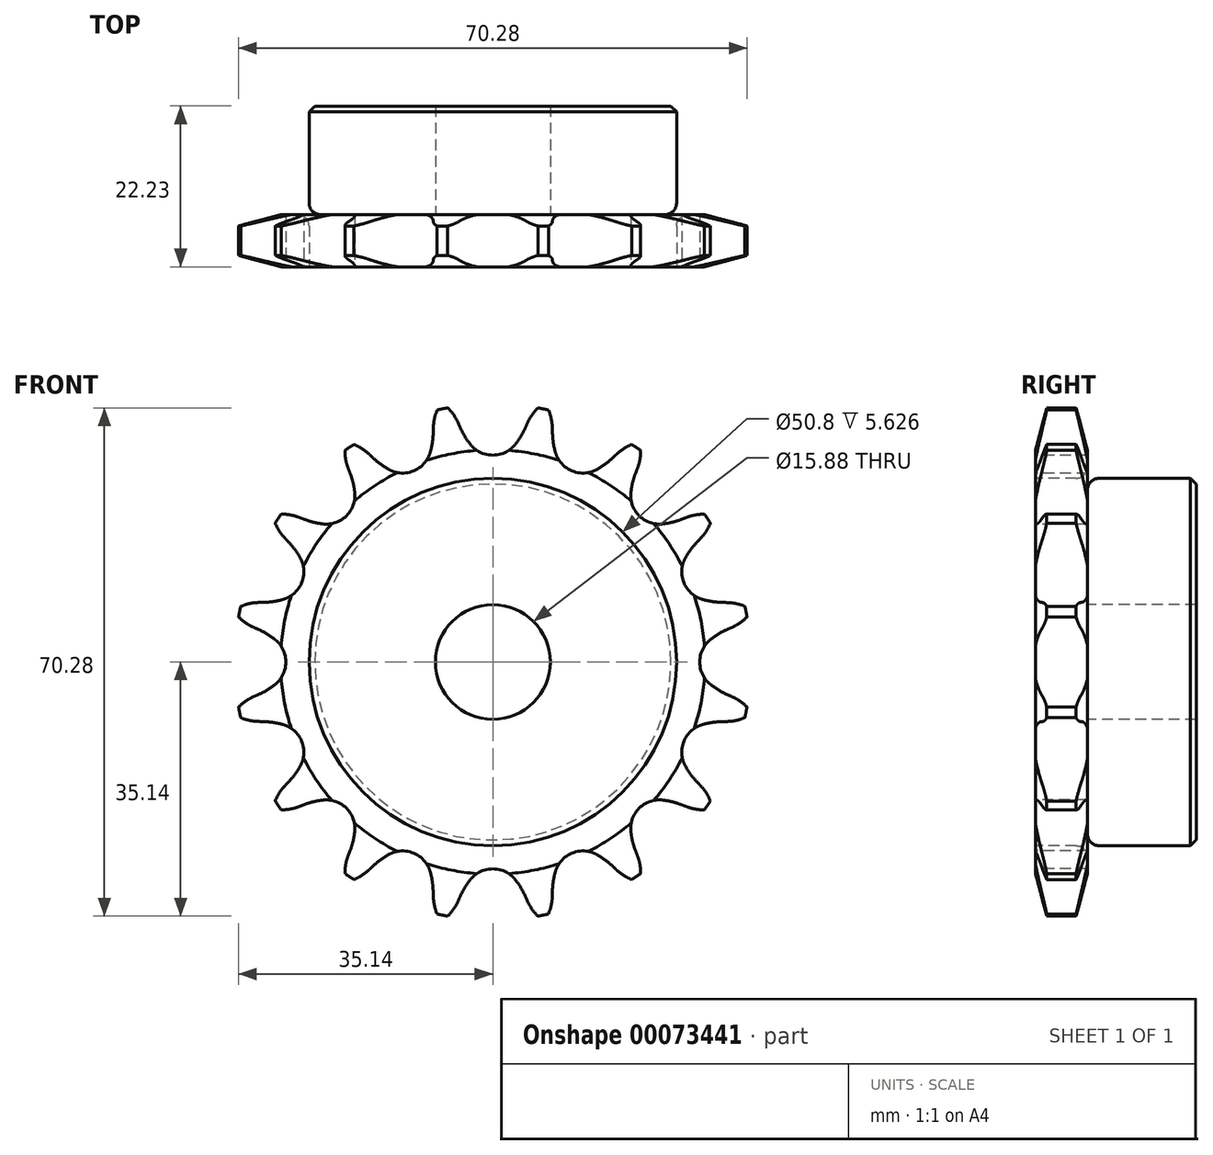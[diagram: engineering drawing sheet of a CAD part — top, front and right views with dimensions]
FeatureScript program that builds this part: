
annotation { "Feature Type Name" : "Feature", "Feature Type Description" : "" }
export const myFeature = defineFeature(function(context is Context, id is Id, definition is map)
    precondition{}
    {
        {
            var Q0;
            Q0=qCreatedBy(makeId("Right.planeOp"),FACE);
            var sketch = newSketch(context, id + "F0", { "sketchPlane" : qUnion([Q0])});
            skLineSegment(sketch, "E0", {"start": v(0, 0) * mm, "end": v(22.23, 0) * mm, "construction": true});
            skLineSegment(sketch, "E1.bottom", {"start": v(0, 7.94) * mm, "end": v(7.21, 7.94) * mm});
            skLineSegment(sketch, "E1.top", {"start": v(0, 35.69) * mm, "end": v(7.21, 35.69) * mm});
            skLineSegment(sketch, "E1.left", {"start": v(0, 7.94) * mm, "end": v(0, 35.69) * mm});
            skLineSegment(sketch, "E1.right", {"start": v(7.21, 7.94) * mm, "end": v(7.21, 35.69) * mm});
            skLineSegment(sketch, "E2.bottom", {"start": v(0, 7.94) * mm, "end": v(22.23, 7.94) * mm});
            skLineSegment(sketch, "E2.top", {"start": v(0, 25.4) * mm, "end": v(22.23, 25.4) * mm});
            skLineSegment(sketch, "E2.left", {"start": v(0, 7.94) * mm, "end": v(0, 25.4) * mm});
            skLineSegment(sketch, "E2.right", {"start": v(22.23, 7.94) * mm, "end": v(22.23, 25.4) * mm});
            skLineSegment(sketch, "E3.MirrorCS", {"start": v(0, -7.94) * mm, "end": v(7.21, -7.94) * mm});
            skLineSegment(sketch, "E4.MirrorCS", {"start": v(0, -25.4) * mm, "end": v(22.23, -25.4) * mm});
            skLineSegment(sketch, "E5.MirrorCS", {"start": v(0, -7.94) * mm, "end": v(22.23, -7.94) * mm});
            skLineSegment(sketch, "E6.MirrorCS", {"start": v(7.21, -7.94) * mm, "end": v(7.21, -35.69) * mm});
            skLineSegment(sketch, "E7.MirrorCS", {"start": v(0, -7.94) * mm, "end": v(0, -35.69) * mm});
            skLineSegment(sketch, "E8.MirrorCS", {"start": v(22.23, -7.94) * mm, "end": v(22.23, -25.4) * mm});
            skLineSegment(sketch, "E9.MirrorCS", {"start": v(0, -7.94) * mm, "end": v(0, -25.4) * mm});
            skLineSegment(sketch, "E10.MirrorCS", {"start": v(0, -35.69) * mm, "end": v(7.21, -35.69) * mm});
            skSolve(sketch);
        }
        {
            var Q0;
            {var subQ0=sQuery(id+"F0.wireOp",EDGE,"E1.top");Q0=makeQuery(id+"F0.imprint","IMPRINT",FACE,{"disambiguationData":[TD([[makeQuery(id+"F0.imprint","IMPRINT",EDGE,{"derivedFrom":subQ0}),-1.0]])]});}
            var Q1;
            {var subQ5=sQuery(id+"F0.wireOp",EDGE,"E2.left");Q1=makeQuery(id+"F0.imprint","IMPRINT",FACE,{"disambiguationData":[TD([[makeQuery(id+"F0.imprint","IMPRINT",EDGE,{"derivedFrom":subQ5}),-1.0]])]});}
            var Q2;
            {var subQ5=sQuery(id+"F0.wireOp",EDGE,"E2.right");Q2=makeQuery(id+"F0.imprint","IMPRINT",FACE,{"disambiguationData":[TD([[makeQuery(id+"F0.imprint","IMPRINT",EDGE,{"derivedFrom":subQ5}),1.0]])]});}
            var Q3;
            Q3=sQuery(id+"F0.wireOp",EDGE,"E0");
            revolve(context, id + "F1", {"entities" : qUnion([Q0, Q1, Q2]), "axis" : qUnion([Q3]), "revolveType" : RevolveType.FULL});
        }
        {
            var Q0;
            Q0=makeQuery(id+"F1.opRevolve","SWEPT_EDGE",EDGE,{"disambiguationData":[OSD([sQuery(id+"F0.wireOp",EDGE,"E1.right"),sQuery(id+"F0.wireOp",EDGE,"E2.top")])]});
            fillet(context, id + "F2", {"entities" : qUnion([Q0]), "radius" : 1.59 * mm, "tangentPropagation" : true, "allowEdgeOverflow" : false});
        }
        {
            var Q0;
            Q0=makeQuery(id+"F1.opRevolve","SWEPT_EDGE",EDGE,{"disambiguationData":[OSD([sQuery(id+"F0.wireOp",EDGE,"E2.top"),sQuery(id+"F0.wireOp",EDGE,"E2.right")])]});
            chamfer(context, id + "F3", {"entities" : qUnion([Q0]), "width" : 0.8 * mm, "tangentPropagation" : true});
        }
        {
            var Q0;
            Q0=makeQuery(id+"F1.opRevolve","SWEPT_EDGE",EDGE,{"disambiguationData":[OSD([sQuery(id+"F0.wireOp",EDGE,"E1.top"),sQuery(id+"F0.wireOp",EDGE,"E1.left")])]});
            var Q1;
            Q1=makeQuery(id+"F1.opRevolve","SWEPT_EDGE",EDGE,{"disambiguationData":[OSD([sQuery(id+"F0.wireOp",EDGE,"E1.top"),sQuery(id+"F0.wireOp",EDGE,"E1.right")])]});
            chamfer(context, id + "F4", {"entities" : qUnion([Q0, Q1]), "chamferType" : ChamferType.TWO_OFFSETS, "width1" : 6.35 * mm, "oppositeDirection" : false, "width2" : 1.57 * mm, "tangentPropagation" : true});
        }
        {
            var Q0;
            Q0=makeQuery(id+"F1.opRevolve","SWEPT_FACE",FACE,{"disambiguationData":[OSD([sQuery(id+"F0.wireOp",EDGE,"E1.left"),sQuery(id+"F0.wireOp",EDGE,"E2.left")])]});
            var sketch = newSketch(context, id + "F5", { "sketchPlane" : qUnion([Q0])});
            skArc(sketch, "E11", {"start": v(-4.8, 33.1) * mm, "mid": v(-5.78, 34.65) * mm, "end": v(-7.13, 35.87) * mm});
            skLineSegment(sketch, "E12", {"start": v(-4.45, 32.3) * mm, "end": v(-4.8, 33.1) * mm});
            skArc(sketch, "E13", {"start": v(-4.45, 32.3) * mm, "mid": v(-3.84, 31.15) * mm, "end": v(-3.1, 30.08) * mm});
            skArc(sketch, "E14", {"start": v(-3.1, 30.08) * mm, "mid": v(0.01, 28.6) * mm, "end": v(3.1, 30.1) * mm});
            skArc(sketch, "E15.MirrorCS", {"start": v(4.46, 32.32) * mm, "mid": v(3.85, 31.17) * mm, "end": v(3.1, 30.1) * mm});
            skLineSegment(sketch, "E16.MirrorCS", {"start": v(4.46, 32.32) * mm, "end": v(4.82, 33.12) * mm});
            skArc(sketch, "E17.MirrorCS", {"start": v(4.82, 33.12) * mm, "mid": v(5.79, 34.66) * mm, "end": v(7.14, 35.87) * mm});
            skLineSegment(sketch, "E18", {"start": v(0, 0) * mm, "end": v(0, 32.56) * mm, "construction": true});
            skArc(sketch, "E19.1.0", {"start": v(-17.1, 28.74) * mm, "mid": v(-18.6, 29.8) * mm, "end": v(-20.32, 30.41) * mm});
            skLineSegment(sketch, "E19.1.1", {"start": v(-16.47, 28.14) * mm, "end": v(-17.1, 28.74) * mm});
            skArc(sketch, "E19.1.2", {"start": v(-16.47, 28.14) * mm, "mid": v(-15.47, 27.3) * mm, "end": v(-14.37, 26.61) * mm});
            skArc(sketch, "E19.1.3", {"start": v(-14.37, 26.61) * mm, "mid": v(-10.93, 26.43) * mm, "end": v(-8.65, 29) * mm});
            skArc(sketch, "E19.1.4", {"start": v(-8.25, 31.57) * mm, "mid": v(-8.37, 30.27) * mm, "end": v(-8.65, 29) * mm});
            skLineSegment(sketch, "E19.1.5", {"start": v(-8.25, 31.57) * mm, "end": v(-8.22, 32.44) * mm});
            skArc(sketch, "E19.1.6", {"start": v(-8.22, 32.44) * mm, "mid": v(-7.91, 34.23) * mm, "end": v(-7.13, 35.87) * mm});
            skArc(sketch, "E19.2.0", {"start": v(-26.8, 20) * mm, "mid": v(-28.59, 20.42) * mm, "end": v(-30.4, 20.32) * mm});
            skLineSegment(sketch, "E19.2.1", {"start": v(-25.99, 19.7) * mm, "end": v(-26.8, 20) * mm});
            skArc(sketch, "E19.2.2", {"start": v(-25.99, 19.7) * mm, "mid": v(-24.74, 19.31) * mm, "end": v(-23.46, 19.09) * mm});
            skArc(sketch, "E19.2.3", {"start": v(-23.46, 19.09) * mm, "mid": v(-20.22, 20.23) * mm, "end": v(-19.09, 23.48) * mm});
            skArc(sketch, "E19.2.4", {"start": v(-19.7, 26.01) * mm, "mid": v(-19.31, 24.76) * mm, "end": v(-19.09, 23.48) * mm});
            skLineSegment(sketch, "E19.2.5", {"start": v(-19.7, 26.01) * mm, "end": v(-20, 26.83) * mm});
            skArc(sketch, "E19.2.6", {"start": v(-20, 26.83) * mm, "mid": v(-20.41, 28.6) * mm, "end": v(-20.32, 30.41) * mm});
            skArc(sketch, "E19.3.0", {"start": v(-32.42, 8.22) * mm, "mid": v(-34.22, 7.92) * mm, "end": v(-35.87, 7.14) * mm});
            skLineSegment(sketch, "E19.3.1", {"start": v(-31.55, 8.25) * mm, "end": v(-32.42, 8.22) * mm});
            skArc(sketch, "E19.3.2", {"start": v(-31.55, 8.25) * mm, "mid": v(-30.25, 8.37) * mm, "end": v(-28.98, 8.66) * mm});
            skArc(sketch, "E19.3.3", {"start": v(-28.98, 8.66) * mm, "mid": v(-26.42, 10.96) * mm, "end": v(-26.62, 14.39) * mm});
            skArc(sketch, "E19.3.4", {"start": v(-28.15, 16.5) * mm, "mid": v(-27.32, 15.49) * mm, "end": v(-26.62, 14.39) * mm});
            skLineSegment(sketch, "E19.3.5", {"start": v(-28.15, 16.5) * mm, "end": v(-28.75, 17.13) * mm});
            skArc(sketch, "E19.3.6", {"start": v(-28.75, 17.13) * mm, "mid": v(-29.8, 18.61) * mm, "end": v(-30.4, 20.32) * mm});
            skArc(sketch, "E19.4.0", {"start": v(-33.1, -4.8) * mm, "mid": v(-34.65, -5.78) * mm, "end": v(-35.87, -7.13) * mm});
            skLineSegment(sketch, "E19.4.1", {"start": v(-32.3, -4.45) * mm, "end": v(-33.1, -4.8) * mm});
            skArc(sketch, "E19.4.2", {"start": v(-32.3, -4.45) * mm, "mid": v(-31.15, -3.84) * mm, "end": v(-30.08, -3.1) * mm});
            skArc(sketch, "E19.4.3", {"start": v(-30.08, -3.1) * mm, "mid": v(-28.6, 0.01) * mm, "end": v(-30.1, 3.1) * mm});
            skArc(sketch, "E19.4.4", {"start": v(-32.32, 4.46) * mm, "mid": v(-31.17, 3.85) * mm, "end": v(-30.1, 3.1) * mm});
            skLineSegment(sketch, "E19.4.5", {"start": v(-32.32, 4.46) * mm, "end": v(-33.12, 4.82) * mm});
            skArc(sketch, "E19.4.6", {"start": v(-33.12, 4.82) * mm, "mid": v(-34.66, 5.79) * mm, "end": v(-35.87, 7.14) * mm});
            skArc(sketch, "E19.5.0", {"start": v(-28.74, -17.1) * mm, "mid": v(-29.8, -18.6) * mm, "end": v(-30.41, -20.32) * mm});
            skLineSegment(sketch, "E19.5.1", {"start": v(-28.14, -16.47) * mm, "end": v(-28.74, -17.1) * mm});
            skArc(sketch, "E19.5.2", {"start": v(-28.14, -16.47) * mm, "mid": v(-27.3, -15.47) * mm, "end": v(-26.61, -14.37) * mm});
            skArc(sketch, "E19.5.3", {"start": v(-26.61, -14.37) * mm, "mid": v(-26.43, -10.93) * mm, "end": v(-29, -8.65) * mm});
            skArc(sketch, "E19.5.4", {"start": v(-31.57, -8.25) * mm, "mid": v(-30.27, -8.37) * mm, "end": v(-29, -8.65) * mm});
            skLineSegment(sketch, "E19.5.5", {"start": v(-31.57, -8.25) * mm, "end": v(-32.44, -8.22) * mm});
            skArc(sketch, "E19.5.6", {"start": v(-32.44, -8.22) * mm, "mid": v(-34.23, -7.91) * mm, "end": v(-35.87, -7.13) * mm});
            skArc(sketch, "E19.6.0", {"start": v(-20, -26.8) * mm, "mid": v(-20.42, -28.59) * mm, "end": v(-20.32, -30.4) * mm});
            skLineSegment(sketch, "E19.6.1", {"start": v(-19.7, -25.99) * mm, "end": v(-20, -26.8) * mm});
            skArc(sketch, "E19.6.2", {"start": v(-19.7, -25.99) * mm, "mid": v(-19.31, -24.74) * mm, "end": v(-19.09, -23.46) * mm});
            skArc(sketch, "E19.6.3", {"start": v(-19.09, -23.46) * mm, "mid": v(-20.23, -20.22) * mm, "end": v(-23.48, -19.09) * mm});
            skArc(sketch, "E19.6.4", {"start": v(-26.01, -19.7) * mm, "mid": v(-24.76, -19.31) * mm, "end": v(-23.48, -19.09) * mm});
            skLineSegment(sketch, "E19.6.5", {"start": v(-26.01, -19.7) * mm, "end": v(-26.83, -20) * mm});
            skArc(sketch, "E19.6.6", {"start": v(-26.83, -20) * mm, "mid": v(-28.6, -20.41) * mm, "end": v(-30.41, -20.32) * mm});
            skArc(sketch, "E19.7.0", {"start": v(-8.22, -32.42) * mm, "mid": v(-7.92, -34.22) * mm, "end": v(-7.14, -35.87) * mm});
            skLineSegment(sketch, "E19.7.1", {"start": v(-8.25, -31.55) * mm, "end": v(-8.22, -32.42) * mm});
            skArc(sketch, "E19.7.2", {"start": v(-8.25, -31.55) * mm, "mid": v(-8.37, -30.25) * mm, "end": v(-8.66, -28.98) * mm});
            skArc(sketch, "E19.7.3", {"start": v(-8.66, -28.98) * mm, "mid": v(-10.96, -26.42) * mm, "end": v(-14.39, -26.62) * mm});
            skArc(sketch, "E19.7.4", {"start": v(-16.5, -28.15) * mm, "mid": v(-15.49, -27.32) * mm, "end": v(-14.39, -26.62) * mm});
            skLineSegment(sketch, "E19.7.5", {"start": v(-16.5, -28.15) * mm, "end": v(-17.13, -28.75) * mm});
            skArc(sketch, "E19.7.6", {"start": v(-17.13, -28.75) * mm, "mid": v(-18.61, -29.8) * mm, "end": v(-20.32, -30.4) * mm});
            skArc(sketch, "E19.8.0", {"start": v(4.8, -33.1) * mm, "mid": v(5.78, -34.65) * mm, "end": v(7.13, -35.87) * mm});
            skLineSegment(sketch, "E19.8.1", {"start": v(4.45, -32.3) * mm, "end": v(4.8, -33.1) * mm});
            skArc(sketch, "E19.8.2", {"start": v(4.45, -32.3) * mm, "mid": v(3.84, -31.15) * mm, "end": v(3.1, -30.08) * mm});
            skArc(sketch, "E19.8.3", {"start": v(3.1, -30.08) * mm, "mid": v(-0.01, -28.6) * mm, "end": v(-3.1, -30.1) * mm});
            skArc(sketch, "E19.8.4", {"start": v(-4.46, -32.32) * mm, "mid": v(-3.85, -31.17) * mm, "end": v(-3.1, -30.1) * mm});
            skLineSegment(sketch, "E19.8.5", {"start": v(-4.46, -32.32) * mm, "end": v(-4.82, -33.12) * mm});
            skArc(sketch, "E19.8.6", {"start": v(-4.82, -33.12) * mm, "mid": v(-5.79, -34.66) * mm, "end": v(-7.14, -35.87) * mm});
            skArc(sketch, "E19.9.0", {"start": v(17.1, -28.74) * mm, "mid": v(18.6, -29.8) * mm, "end": v(20.32, -30.41) * mm});
            skLineSegment(sketch, "E19.9.1", {"start": v(16.47, -28.14) * mm, "end": v(17.1, -28.74) * mm});
            skArc(sketch, "E19.9.2", {"start": v(16.47, -28.14) * mm, "mid": v(15.47, -27.3) * mm, "end": v(14.37, -26.61) * mm});
            skArc(sketch, "E19.9.3", {"start": v(14.37, -26.61) * mm, "mid": v(10.93, -26.43) * mm, "end": v(8.65, -29) * mm});
            skArc(sketch, "E19.9.4", {"start": v(8.25, -31.57) * mm, "mid": v(8.37, -30.27) * mm, "end": v(8.65, -29) * mm});
            skLineSegment(sketch, "E19.9.5", {"start": v(8.25, -31.57) * mm, "end": v(8.22, -32.44) * mm});
            skArc(sketch, "E19.9.6", {"start": v(8.22, -32.44) * mm, "mid": v(7.91, -34.23) * mm, "end": v(7.13, -35.87) * mm});
            skArc(sketch, "E19.10.0", {"start": v(26.8, -20) * mm, "mid": v(28.59, -20.42) * mm, "end": v(30.4, -20.32) * mm});
            skLineSegment(sketch, "E19.10.1", {"start": v(25.99, -19.7) * mm, "end": v(26.8, -20) * mm});
            skArc(sketch, "E19.10.2", {"start": v(25.99, -19.7) * mm, "mid": v(24.74, -19.31) * mm, "end": v(23.46, -19.09) * mm});
            skArc(sketch, "E19.10.3", {"start": v(23.46, -19.09) * mm, "mid": v(20.22, -20.23) * mm, "end": v(19.09, -23.48) * mm});
            skArc(sketch, "E19.10.4", {"start": v(19.7, -26.01) * mm, "mid": v(19.31, -24.76) * mm, "end": v(19.09, -23.48) * mm});
            skLineSegment(sketch, "E19.10.5", {"start": v(19.7, -26.01) * mm, "end": v(20, -26.83) * mm});
            skArc(sketch, "E19.10.6", {"start": v(20, -26.83) * mm, "mid": v(20.41, -28.6) * mm, "end": v(20.32, -30.41) * mm});
            skArc(sketch, "E19.11.0", {"start": v(32.42, -8.22) * mm, "mid": v(34.22, -7.92) * mm, "end": v(35.87, -7.14) * mm});
            skLineSegment(sketch, "E19.11.1", {"start": v(31.55, -8.25) * mm, "end": v(32.42, -8.22) * mm});
            skArc(sketch, "E19.11.2", {"start": v(31.55, -8.25) * mm, "mid": v(30.25, -8.37) * mm, "end": v(28.98, -8.66) * mm});
            skArc(sketch, "E19.11.3", {"start": v(28.98, -8.66) * mm, "mid": v(26.42, -10.96) * mm, "end": v(26.62, -14.39) * mm});
            skArc(sketch, "E19.11.4", {"start": v(28.15, -16.5) * mm, "mid": v(27.32, -15.49) * mm, "end": v(26.62, -14.39) * mm});
            skLineSegment(sketch, "E19.11.5", {"start": v(28.15, -16.5) * mm, "end": v(28.75, -17.13) * mm});
            skArc(sketch, "E19.11.6", {"start": v(28.75, -17.13) * mm, "mid": v(29.8, -18.61) * mm, "end": v(30.4, -20.32) * mm});
            skArc(sketch, "E19.12.0", {"start": v(33.1, 4.8) * mm, "mid": v(34.65, 5.78) * mm, "end": v(35.87, 7.13) * mm});
            skLineSegment(sketch, "E19.12.1", {"start": v(32.3, 4.45) * mm, "end": v(33.1, 4.8) * mm});
            skArc(sketch, "E19.12.2", {"start": v(32.3, 4.45) * mm, "mid": v(31.15, 3.84) * mm, "end": v(30.08, 3.1) * mm});
            skArc(sketch, "E19.12.3", {"start": v(30.08, 3.1) * mm, "mid": v(28.6, -0.01) * mm, "end": v(30.1, -3.1) * mm});
            skArc(sketch, "E19.12.4", {"start": v(32.32, -4.46) * mm, "mid": v(31.17, -3.85) * mm, "end": v(30.1, -3.1) * mm});
            skLineSegment(sketch, "E19.12.5", {"start": v(32.32, -4.46) * mm, "end": v(33.12, -4.82) * mm});
            skArc(sketch, "E19.12.6", {"start": v(33.12, -4.82) * mm, "mid": v(34.66, -5.79) * mm, "end": v(35.87, -7.14) * mm});
            skArc(sketch, "E19.13.0", {"start": v(28.74, 17.1) * mm, "mid": v(29.8, 18.6) * mm, "end": v(30.41, 20.32) * mm});
            skLineSegment(sketch, "E19.13.1", {"start": v(28.14, 16.47) * mm, "end": v(28.74, 17.1) * mm});
            skArc(sketch, "E19.13.2", {"start": v(28.14, 16.47) * mm, "mid": v(27.3, 15.47) * mm, "end": v(26.61, 14.37) * mm});
            skArc(sketch, "E19.13.3", {"start": v(26.61, 14.37) * mm, "mid": v(26.43, 10.93) * mm, "end": v(29, 8.65) * mm});
            skArc(sketch, "E19.13.4", {"start": v(31.57, 8.25) * mm, "mid": v(30.27, 8.37) * mm, "end": v(29, 8.65) * mm});
            skLineSegment(sketch, "E19.13.5", {"start": v(31.57, 8.25) * mm, "end": v(32.44, 8.22) * mm});
            skArc(sketch, "E19.13.6", {"start": v(32.44, 8.22) * mm, "mid": v(34.23, 7.91) * mm, "end": v(35.87, 7.13) * mm});
            skArc(sketch, "E19.14.0", {"start": v(20, 26.8) * mm, "mid": v(20.42, 28.59) * mm, "end": v(20.32, 30.4) * mm});
            skLineSegment(sketch, "E19.14.1", {"start": v(19.7, 25.99) * mm, "end": v(20, 26.8) * mm});
            skArc(sketch, "E19.14.2", {"start": v(19.7, 25.99) * mm, "mid": v(19.31, 24.74) * mm, "end": v(19.09, 23.46) * mm});
            skArc(sketch, "E19.14.3", {"start": v(19.09, 23.46) * mm, "mid": v(20.23, 20.22) * mm, "end": v(23.48, 19.09) * mm});
            skArc(sketch, "E19.14.4", {"start": v(26.01, 19.7) * mm, "mid": v(24.76, 19.31) * mm, "end": v(23.48, 19.09) * mm});
            skLineSegment(sketch, "E19.14.5", {"start": v(26.01, 19.7) * mm, "end": v(26.83, 20) * mm});
            skArc(sketch, "E19.14.6", {"start": v(26.83, 20) * mm, "mid": v(28.6, 20.41) * mm, "end": v(30.41, 20.32) * mm});
            skArc(sketch, "E19.15.0", {"start": v(8.22, 32.42) * mm, "mid": v(7.92, 34.22) * mm, "end": v(7.14, 35.87) * mm});
            skLineSegment(sketch, "E19.15.1", {"start": v(8.25, 31.55) * mm, "end": v(8.22, 32.42) * mm});
            skArc(sketch, "E19.15.2", {"start": v(8.25, 31.55) * mm, "mid": v(8.37, 30.25) * mm, "end": v(8.66, 28.98) * mm});
            skArc(sketch, "E19.15.3", {"start": v(8.66, 28.98) * mm, "mid": v(10.96, 26.42) * mm, "end": v(14.39, 26.62) * mm});
            skArc(sketch, "E19.15.4", {"start": v(16.5, 28.15) * mm, "mid": v(15.49, 27.32) * mm, "end": v(14.39, 26.62) * mm});
            skLineSegment(sketch, "E19.15.5", {"start": v(16.5, 28.15) * mm, "end": v(17.13, 28.75) * mm});
            skArc(sketch, "E19.15.6", {"start": v(17.13, 28.75) * mm, "mid": v(18.61, 29.8) * mm, "end": v(20.32, 30.4) * mm});
            skPoint(sketch, "E19.center", {"position": v(0, 0) * mm});
            skSolve(sketch);
        }
        {
            var Q0;
            Q0 = qSketchRegion(id + "F5", true);
            extrude(context, id + "F6", {"entities" : qUnion([Q0]), "operationType" : NewBodyOperationType.INTERSECT, "endBound" : BoundingType.THROUGH_ALL, "oppositeDirection" : true, "depth" : 25.4 * mm});
        }
    });
